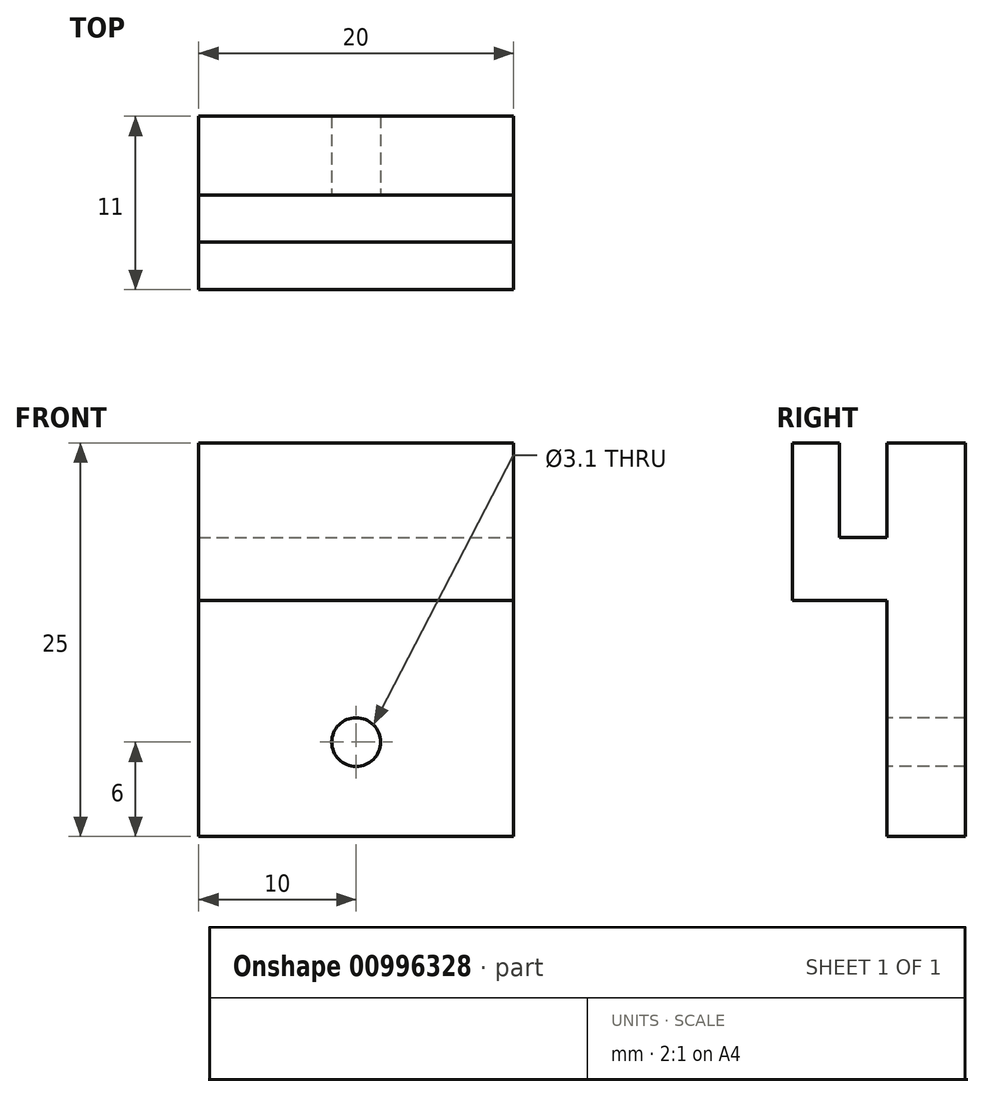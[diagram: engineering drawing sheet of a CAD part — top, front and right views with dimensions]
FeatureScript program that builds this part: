
annotation { "Feature Type Name" : "Feature", "Feature Type Description" : "" }
export const myFeature = defineFeature(function(context is Context, id is Id, definition is map)
    precondition{}
    {
        {
            var Q0;
            Q0=qCreatedBy(makeId("Front.planeOp"),FACE);
            var sketch = newSketch(context, id + "F0", { "sketchPlane" : qUnion([Q0])});
            skLineSegment(sketch, "E0.bottom", {"start": v(-10, 12.5) * mm, "end": v(10, 12.5) * mm});
            skLineSegment(sketch, "E0.top", {"start": v(-10, -12.5) * mm, "end": v(10, -12.5) * mm});
            skLineSegment(sketch, "E0.left", {"start": v(-10, 12.5) * mm, "end": v(-10, -12.5) * mm});
            skLineSegment(sketch, "E0.right", {"start": v(10, 12.5) * mm, "end": v(10, -12.5) * mm});
            skPoint(sketch, "E0.middle", {"position": v(0, 0) * mm});
            skSolve(sketch);
        }
        {
            var Q0;
            Q0=makeQuery(id+"F0.imprint","IMPRINT",FACE,{"disambiguationData":[TD([[makeQuery(id+"F0.imprint","IMPRINT",EDGE,{"derivedFrom":sQuery(id+"F0.wireOp",EDGE,"E0.bottom")}),-1.0]])]});
            extrude(context, id + "F1", {"entities" : qUnion([Q0]), "depth" : 5 * mm, "offsetDistance" : 25 * mm});
        }
        {
            var Q0;
            Q0=makeQuery(id+"F1.opExtrude","CAP_FACE",FACE,{"disambiguationData":[OSD([sQuery(id+"F0.wireOp",EDGE,"E0.bottom"),sQuery(id+"F0.wireOp",EDGE,"E0.top"),sQuery(id+"F0.wireOp",EDGE,"E0.left"),sQuery(id+"F0.wireOp",EDGE,"E0.right")])],"isStart":false});
            var sketch = newSketch(context, id + "F2", { "sketchPlane" : qUnion([Q0])});
            skLineSegment(sketch, "E1", {"start": v(-10, 12.5) * mm, "end": v(-10, 6.5) * mm});
            skLineSegment(sketch, "E2.bottom", {"start": v(-10, 6.5) * mm, "end": v(10, 6.5) * mm});
            skLineSegment(sketch, "E2.top", {"start": v(-10, 2.5) * mm, "end": v(10, 2.5) * mm});
            skLineSegment(sketch, "E2.left", {"start": v(-10, 6.5) * mm, "end": v(-10, 2.5) * mm});
            skLineSegment(sketch, "E2.right", {"start": v(10, 6.5) * mm, "end": v(10, 2.5) * mm});
            skSolve(sketch);
        }
        {
            var Q0;
            Q0=makeQuery(id+"F2.imprint","IMPRINT",FACE,{"disambiguationData":[TD([[makeQuery(id+"F2.imprint","IMPRINT",EDGE,{"derivedFrom":sQuery(id+"F2.wireOp",EDGE,"E2.bottom")}),-1.0]])]});
            extrude(context, id + "F3", {"entities" : qUnion([Q0]), "operationType" : NewBodyOperationType.ADD, "depth" : 3 * mm, "offsetDistance" : 25 * mm});
        }
        {
            var Q0;
            Q0=makeQuery(id+"F3.opExtrude","CAP_FACE",FACE,{"disambiguationData":[OSD([sQuery(id+"F2.wireOp",EDGE,"E2.bottom"),sQuery(id+"F2.wireOp",EDGE,"E2.top"),sQuery(id+"F2.wireOp",EDGE,"E2.left"),sQuery(id+"F2.wireOp",EDGE,"E2.right")])],"isStart":false});
            var sketch = newSketch(context, id + "F4", { "sketchPlane" : qUnion([Q0])});
            skLineSegment(sketch, "E3.bottom", {"start": v(-10, 2.5) * mm, "end": v(10, 2.5) * mm});
            skLineSegment(sketch, "E3.top", {"start": v(-10, 12.5) * mm, "end": v(10, 12.5) * mm});
            skLineSegment(sketch, "E3.left", {"start": v(-10, 2.5) * mm, "end": v(-10, 12.5) * mm});
            skLineSegment(sketch, "E3.right", {"start": v(10, 2.5) * mm, "end": v(10, 12.5) * mm});
            skSolve(sketch);
        }
        {
            var Q0;
            {var subQ0=sQuery(id+"F4.wireOp",EDGE,"E3.bottom");Q0=makeQuery(id+"F4.imprint","IMPRINT",FACE,{"disambiguationData":[TD([[makeQuery(id+"F4.imprint","IMPRINT",EDGE,{"derivedFrom":subQ0}),1.0]])]});}
            var Q1;
            {var subQ0=sQuery(id+"F4.wireOp",EDGE,"E3.top");Q1=makeQuery(id+"F4.imprint","IMPRINT",FACE,{"disambiguationData":[TD([[makeQuery(id+"F4.imprint","IMPRINT",EDGE,{"derivedFrom":subQ0}),-1.0]])]});}
            extrude(context, id + "F5", {"entities" : qUnion([Q0, Q1]), "operationType" : NewBodyOperationType.ADD, "depth" : 3 * mm, "offsetDistance" : 25 * mm});
        }
        {
            var Q0;
            {var subQ0=sQuery(id+"F0.wireOp",EDGE,"E0.left");var subQ1=sQuery(id+"F0.wireOp",EDGE,"E0.right");var subQ2=sQuery(id+"F0.wireOp",EDGE,"E0.top");Q0=makeQuery(id+"F3.boolean.opBoolean","SPLIT",FACE,{"disambiguationData":[TD([makeQuery(id+"F1.opExtrude","SWEPT_FACE",FACE,{"disambiguationData":[OSD([subQ2])]})])],"derivedFrom":makeQuery(id+"F1.opExtrude","CAP_FACE",FACE,{"disambiguationData":[OSD([sQuery(id+"F0.wireOp",EDGE,"E0.bottom"),subQ2,subQ0,subQ1])],"isStart":false})});}
            var sketch = newSketch(context, id + "F6", { "sketchPlane" : qUnion([Q0])});
            skLineSegment(sketch, "E4", {"start": v(0, -12.5) * mm, "end": v(0, -6.5) * mm});
            skCircle(sketch, "E5", {"center": v(0, -6.5) * mm, "radius": 1.55 * mm});
            skSolve(sketch);
        }
        {
            var Q0;
            Q0=makeQuery(id+"F6.imprint","IMPRINT",FACE,{"disambiguationData":[TD([[makeQuery(id+"F6.imprint","IMPRINT",EDGE,{"derivedFrom":sQuery(id+"F6.wireOp",EDGE,"E5")}),1.0]])]});
            extrude(context, id + "F7", {"entities" : qUnion([Q0]), "operationType" : NewBodyOperationType.REMOVE, "oppositeDirection" : true, "depth" : 25 * mm, "offsetDistance" : 25 * mm});
        }
    });
